# Revit family: Gorter BV THERMO 1000x600mm
name_source: partatom
category: Generic Models
units: mm (PartAtom-declared; Revit-internal decimal feet)

## family parameters
Can host rebar = No
Cut with Voids When Loaded = Yes
Host = Face
Part Type = Normal
Room Calculation Point = No
Round Connector Dimension = Use Diameter
Shared = No

## types (5) — shared parameters
Default Elevation = 1219 mm
Manufacturer = Gorter
Model = BV THERMO
RC-waarde = 3.2 m2 K/W
belasting = 125 kN
binnenluik = tbv betonvulling
brandwerend 90 min = nee
gasdrukveer = nee
geïsoleerd = ja
materiaal = bcb_staal
rubberen_afdichting = enkel
scharnierend = nee
sluiting = 4
vergrendeling = nee
vullen_met_beton = ja

## per-type parameters (varying)
| type | Description | binnenmaat_breedte | binnenmaat_lengte | gewicht | uitwendige_breedte | uitwendige_lengte |
| BV THERMO 600x600mm | BV THERMO 66 | 600 mm | 600 mm | 23 | 735 mm | 735 mm |
| BV THERMO 800x600mm | BV THERMO 86 | 600 mm | 800 mm  [stored 2.62467 ft] | 29 | 735 mm | 935 mm |
| BV THERMO 800x800mm | BV THERMO 88 | 800 mm  [stored 2.62467 ft] | 800 mm  [stored 2.62467 ft] | 33 | 935 mm | 935 mm |
| BV THERMO 1000x600mm | BV THERMO 106 | 600 mm | 1000 mm  [stored 3.28084 ft] | 33 | 735 mm | 1135 mm  [stored 3.72375 ft] |
| BV THERMO 600x400mm | BV THERMO 64 | 400 mm  [stored 1.31234 ft] | 600 mm | 23 | 535 mm  [stored 1.75525 ft] | 735 mm |

note: [stored X ft] marks values corroborated as IEEE doubles in the binary element streams (Revit-internal decimal feet)

## geometry (parser evidence)
native form markers: Sweep x10
no freeform markers — native parametric forms only
